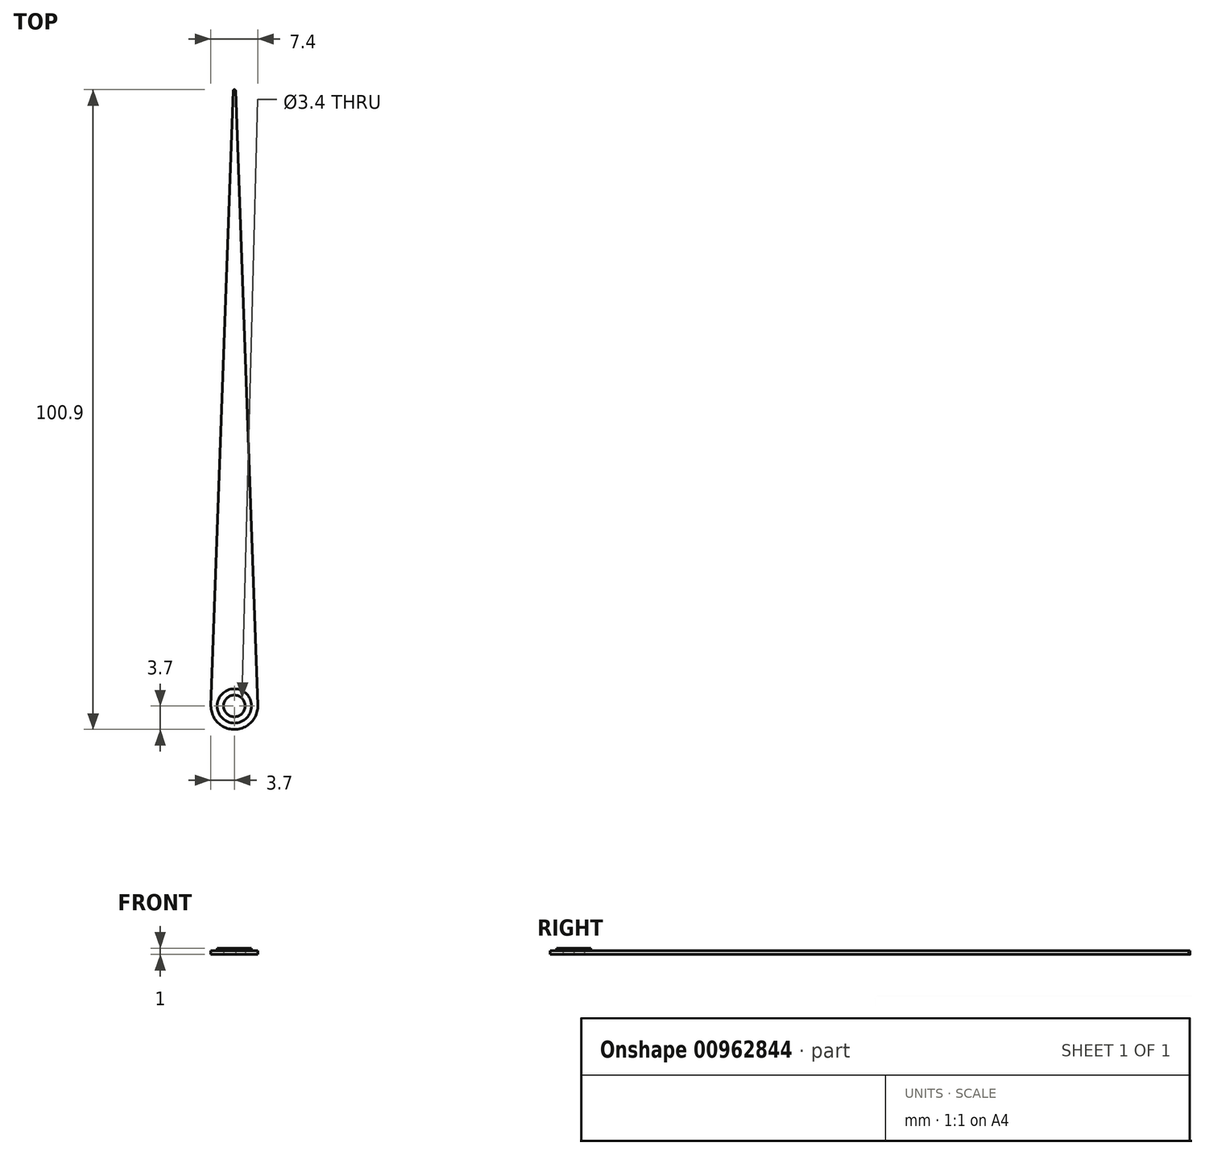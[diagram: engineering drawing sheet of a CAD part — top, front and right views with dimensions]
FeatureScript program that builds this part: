
annotation { "Feature Type Name" : "Feature", "Feature Type Description" : "" }
export const myFeature = defineFeature(function(context is Context, id is Id, definition is map)
    precondition{}
    {
        {
            var Q0;
            Q0=qCreatedBy(makeId("Top.planeOp"),FACE);
            var sketch = newSketch(context, id + "F0", { "sketchPlane" : qUnion([Q0])});
            skCircle(sketch, "E0", {"center": v(0, 0) * mm, "radius": 1.7 * mm});
            skCircle(sketch, "E1", {"center": v(0, 0) * mm, "radius": 3.7 * mm});
            skPoint(sketch, "E2", {"position": v(0, 97) * mm});
            skCircle(sketch, "E3", {"center": v(0, 97) * mm, "radius": 0.2 * mm});
            skLineSegment(sketch, "E4", {"start": v(0.2, 97) * mm, "end": v(3.7, 0) * mm});
            skLineSegment(sketch, "E5", {"start": v(-3.7, 0) * mm, "end": v(-0.2, 97) * mm});
            skSolve(sketch);
        }
        {
            var Q0;
            {var subQ0=sQuery(id+"F0.wireOp",EDGE,"E4");var subQ1=sQuery(id+"F0.wireOp",EDGE,"E1");var subQ2=makeQuery(id+"F0.imprint","INTERSECT",VERTEX,{"derivedFrom":[subQ1,subQ0]});Q0=makeQuery(id+"F0.imprint","IMPRINT",FACE,{"disambiguationData":[TD([[makeQuery(id+"F0.imprint","IMPRINT",EDGE,{"disambiguationData":[TD([[subQ2,-1.0]])],"derivedFrom":subQ1}),-1.0]])]});}
            var Q1;
            Q1=makeQuery(id+"F0.imprint","IMPRINT",FACE,{"disambiguationData":[TD([[makeQuery(id+"F0.imprint","IMPRINT",EDGE,{"derivedFrom":sQuery(id+"F0.wireOp",EDGE,"E0")}),-1.0]])]});
            var Q2;
            {var subQ0=sQuery(id+"F0.wireOp",EDGE,"E3");var subQ1=makeQuery(id+"F0.imprint","INTERSECT",VERTEX,{"derivedFrom":[subQ0,sQuery(id+"F0.wireOp",EDGE,"E4")]});Q2=makeQuery(id+"F0.imprint","IMPRINT",FACE,{"disambiguationData":[TD([[makeQuery(id+"F0.imprint","IMPRINT",EDGE,{"disambiguationData":[TD([[subQ1,-1.0]])],"derivedFrom":subQ0}),1.0]])]});}
            extrude(context, id + "F1", {"entities" : qUnion([Q0, Q1, Q2]), "depth" : 0.6 * mm, "offsetDistance" : 25 * mm});
        }
        {
            var Q0;
            Q0=makeQuery(id+"F1.opExtrude","CAP_FACE",FACE,{"disambiguationData":[OSD([sQuery(id+"F0.wireOp",EDGE,"E0"),sQuery(id+"F0.wireOp",EDGE,"E1"),sQuery(id+"F0.wireOp",EDGE,"E3"),sQuery(id+"F0.wireOp",EDGE,"E4"),sQuery(id+"F0.wireOp",EDGE,"E5")])],"isStart":false});
            var sketch = newSketch(context, id + "F2", { "sketchPlane" : qUnion([Q0])});
            skCircle(sketch, "E6", {"center": v(0, 0) * mm, "radius": 1.7 * mm});
            skCircle(sketch, "E7", {"center": v(0, 0) * mm, "radius": 2.7 * mm});
            skSolve(sketch);
        }
        {
            var Q0;
            Q0=makeQuery(id+"F2.imprint","IMPRINT",FACE,{"disambiguationData":[TD([[makeQuery(id+"F2.imprint","IMPRINT",EDGE,{"derivedFrom":sQuery(id+"F2.wireOp",EDGE,"E6")}),-1.0]])]});
            extrude(context, id + "F3", {"entities" : qUnion([Q0]), "operationType" : NewBodyOperationType.ADD, "depth" : 0.4 * mm, "offsetDistance" : 25 * mm});
        }
    });
